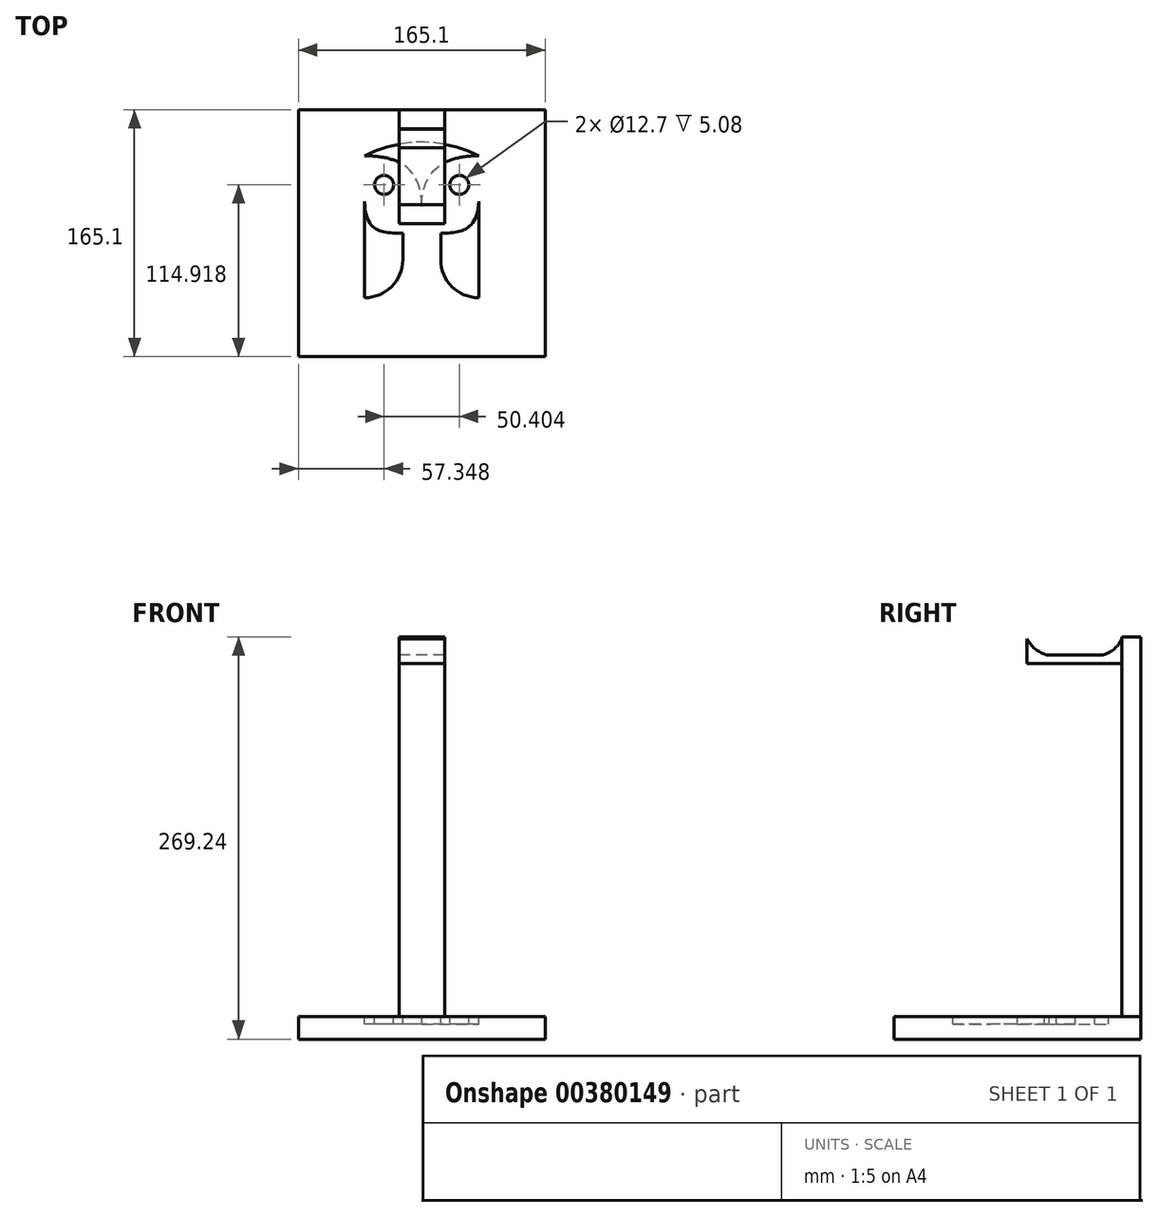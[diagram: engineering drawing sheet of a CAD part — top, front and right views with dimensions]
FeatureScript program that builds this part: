
annotation { "Feature Type Name" : "Feature", "Feature Type Description" : "" }
export const myFeature = defineFeature(function(context is Context, id is Id, definition is map)
    precondition{}
    {
        {
            var Q0;
            Q0=qCreatedBy(makeId("Front.planeOp"),FACE);
            var sketch = newSketch(context, id + "F0", { "sketchPlane" : qUnion([Q0])});
            skLineSegment(sketch, "E0.bottom", {"start": v(82.55, 7.62) * mm, "end": v(-82.55, 7.62) * mm});
            skLineSegment(sketch, "E0.top", {"start": v(82.55, -7.62) * mm, "end": v(-82.55, -7.62) * mm});
            skLineSegment(sketch, "E0.left", {"start": v(82.55, 7.62) * mm, "end": v(82.55, -7.62) * mm});
            skLineSegment(sketch, "E0.right", {"start": v(-82.55, 7.62) * mm, "end": v(-82.55, -7.62) * mm});
            skPoint(sketch, "E0.middle", {"position": v(0, 0) * mm});
            skSolve(sketch);
        }
        {
            var Q0;
            Q0 = qSketchRegion(id + "F0", true);
            extrude(context, id + "F1", {"entities" : qUnion([Q0]), "endBound" : BoundingType.SYMMETRIC, "oppositeDirection" : true, "depth" : 165.1 * mm});
        }
        {
            var Q0;
            Q0=makeQuery(id+"F1.opExtrude","SWEPT_FACE",FACE,{"disambiguationData":[OSD([sQuery(id+"F0.wireOp",EDGE,"E0.bottom")])]});
            var sketch = newSketch(context, id + "F2", { "sketchPlane" : qUnion([Q0])});
            skLineSegment(sketch, "E1.bottom", {"start": v(-15.24, 82.55) * mm, "end": v(15.24, 82.55) * mm});
            skLineSegment(sketch, "E1.top", {"start": v(-15.24, 69.85) * mm, "end": v(15.24, 69.85) * mm});
            skLineSegment(sketch, "E1.left", {"start": v(-15.24, 82.55) * mm, "end": v(-15.24, 69.85) * mm});
            skLineSegment(sketch, "E1.right", {"start": v(15.24, 82.55) * mm, "end": v(15.24, 69.85) * mm});
            skLineSegment(sketch, "E2.bottom", {"start": v(-38.1, 0) * mm, "end": v(-12.7, 0) * mm});
            skLineSegment(sketch, "E2.top", {"start": v(-38.1, -17.78) * mm, "end": v(-12.7, -17.78) * mm});
            skLineSegment(sketch, "E2.left", {"start": v(-38.1, 0) * mm, "end": v(-38.1, -17.78) * mm});
            skLineSegment(sketch, "E2.right", {"start": v(-12.7, 0) * mm, "end": v(-12.7, -17.78) * mm});
            skLineSegment(sketch, "E3.bottom", {"start": v(12.7, 0) * mm, "end": v(38.1, 0) * mm});
            skLineSegment(sketch, "E3.top", {"start": v(12.7, -17.78) * mm, "end": v(38.1, -17.78) * mm});
            skLineSegment(sketch, "E3.left", {"start": v(12.7, 0) * mm, "end": v(12.7, -17.78) * mm});
            skLineSegment(sketch, "E3.right", {"start": v(38.1, 0) * mm, "end": v(38.1, -17.78) * mm});
            skArc(sketch, "E4", {"start": v(-12.7, -17.78) * mm, "mid": v(-20.14, -35.74) * mm, "end": v(-38.1, -43.18) * mm});
            skLineSegment(sketch, "E5", {"start": v(-38.1, -17.78) * mm, "end": v(-38.1, -43.18) * mm});
            skArc(sketch, "E6", {"start": v(12.7, -17.78) * mm, "mid": v(20.14, -35.74) * mm, "end": v(38.1, -43.18) * mm});
            skLineSegment(sketch, "E7", {"start": v(38.1, -17.78) * mm, "end": v(38.1, -43.18) * mm});
            skLineSegment(sketch, "E8", {"start": v(38.1, 0) * mm, "end": v(38.1, 21.23) * mm});
            skLineSegment(sketch, "E9", {"start": v(-38.1, 0) * mm, "end": v(-38.1, 21.23) * mm});
            skFitSpline(sketch, "E10", {"points": [v(-12.7, 0) * mm, v(-38.1, 21.23) * mm], "startDerivative": vector(-38.1, 0) * mm, "endDerivative": vector(0, 63.68) * mm});
            skFitSpline(sketch, "E11", {"points": [v(38.1, 21.23) * mm, v(12.7, 0) * mm], "startDerivative": vector(0, -63.68) * mm, "endDerivative": vector(-27.64, 0) * mm});
            skLineSegment(sketch, "E12", {"start": v(-10.78, 17.94) * mm, "end": v(0, 7.17) * mm});
            skLineSegment(sketch, "E13", {"start": v(0, 7.17) * mm, "end": v(10.78, 17.94) * mm});
            skLineSegment(sketch, "E14", {"start": v(-10.78, 17.94) * mm, "end": v(10.78, 17.94) * mm});
            skCircle(sketch, "E15", {"center": v(25.2, 32.37) * mm, "radius": 6.35 * mm});
            skCircle(sketch, "E16", {"center": v(-25.2, 32.37) * mm, "radius": 6.35 * mm});
            skPoint(sketch, "E17", {"position": v(0, 17.94) * mm});
            skPoint(sketch, "E18", {"position": v(38.1, 51.82) * mm});
            skPoint(sketch, "E19", {"position": v(-38.1, 51.82) * mm});
            skFitSpline(sketch, "E20", {"points": [v(0, 17.94) * mm, v(-38.1, 51.82) * mm], "startDerivative": vector(0, 62.62) * mm, "endDerivative": vector(-84.2, 0) * mm});
            skFitSpline(sketch, "E21", {"points": [v(0, 17.94) * mm, v(38.1, 51.82) * mm], "startDerivative": vector(0, 62.62) * mm, "endDerivative": vector(80.13, 0) * mm});
            skArc(sketch, "E22", {"start": v(38.1, 51.82) * mm, "mid": v(0, 60.9) * mm, "end": v(-38.1, 51.82) * mm});
            skSolve(sketch);
        }
        {
            var Q0;
            Q0=makeQuery(id+"F2.imprint","IMPRINT",FACE,{"disambiguationData":[TD([[makeQuery(id+"F2.imprint","IMPRINT",EDGE,{"derivedFrom":sQuery(id+"F2.wireOp",EDGE,"E1.bottom")}),1.0]])]});
            extrude(context, id + "F3", {"entities" : qUnion([Q0]), "operationType" : NewBodyOperationType.ADD, "depth" : 254 * mm});
        }
        {
            var Q0;
            Q0=qCreatedBy(makeId("Right.planeOp"),FACE);
            var sketch = newSketch(context, id + "F4", { "sketchPlane" : qUnion([Q0])});
            skLineSegment(sketch, "E23.bottom", {"start": v(69.82, 249.55) * mm, "end": v(6.32, 249.55) * mm});
            skLineSegment(sketch, "E23.top", {"start": v(69.82, 243.6) * mm, "end": v(6.32, 243.6) * mm});
            skLineSegment(sketch, "E23.left", {"start": v(69.82, 249.55) * mm, "end": v(69.82, 243.6) * mm});
            skLineSegment(sketch, "E23.right", {"start": v(6.32, 249.55) * mm, "end": v(6.32, 243.6) * mm});
            skPoint(sketch, "E24", {"position": v(69.67, 260.1) * mm});
            skLineSegment(sketch, "E25", {"start": v(6.32, 249.55) * mm, "end": v(6.32, 260.1) * mm});
            skPoint(sketch, "E26", {"position": v(19.02, 249.55) * mm});
            skPoint(sketch, "E27", {"position": v(57.12, 249.55) * mm});
            skArc(sketch, "E28", {"start": v(57.12, 249.55) * mm, "mid": v(64.62, 253.37) * mm, "end": v(69.67, 260.1) * mm});
            skArc(sketch, "E29", {"start": v(6.32, 260.1) * mm, "mid": v(11.7, 253.65) * mm, "end": v(19.02, 249.55) * mm});
            skLineSegment(sketch, "E30", {"start": v(69.67, 260.1) * mm, "end": v(69.82, 249.55) * mm});
            skSolve(sketch);
        }
        {
            var Q0;
            Q0 = qSketchRegion(id + "F4", true);
            extrude(context, id + "F5", {"entities" : qUnion([Q0]), "endBound" : BoundingType.SYMMETRIC, "depth" : 30.48 * mm});
        }
        {
            var Q0;
            {var subQ0=sQuery(id+"F2.wireOp",EDGE,"E20");Q0=makeQuery(id+"F2.imprint","IMPRINT",FACE,{"disambiguationData":[TD([[makeQuery(id+"F2.imprint","IMPRINT",EDGE,{"derivedFrom":subQ0}),-1.0]])]});}
            var Q1;
            Q1=makeQuery(id+"F2.imprint","IMPRINT",FACE,{"disambiguationData":[TD([[makeQuery(id+"F2.imprint","IMPRINT",EDGE,{"derivedFrom":sQuery(id+"F2.wireOp",EDGE,"E16")}),1.0]])]});
            var Q2;
            Q2=makeQuery(id+"F2.imprint","IMPRINT",FACE,{"disambiguationData":[TD([[makeQuery(id+"F2.imprint","IMPRINT",EDGE,{"derivedFrom":sQuery(id+"F2.wireOp",EDGE,"E15")}),1.0]])]});
            var Q3;
            Q3=makeQuery(id+"F2.imprint","IMPRINT",FACE,{"disambiguationData":[TD([[makeQuery(id+"F2.imprint","IMPRINT",EDGE,{"derivedFrom":sQuery(id+"F2.wireOp",EDGE,"E2.bottom")}),-1.0]])]});
            var Q4;
            Q4=makeQuery(id+"F2.imprint","IMPRINT",FACE,{"disambiguationData":[TD([[makeQuery(id+"F2.imprint","IMPRINT",EDGE,{"derivedFrom":sQuery(id+"F2.wireOp",EDGE,"E2.top")}),-1.0]])]});
            var Q5;
            Q5=makeQuery(id+"F2.imprint","IMPRINT",FACE,{"disambiguationData":[TD([[makeQuery(id+"F2.imprint","IMPRINT",EDGE,{"derivedFrom":sQuery(id+"F2.wireOp",EDGE,"E2.bottom")}),1.0]])]});
            var Q6;
            Q6=makeQuery(id+"F2.imprint","IMPRINT",FACE,{"disambiguationData":[TD([[makeQuery(id+"F2.imprint","IMPRINT",EDGE,{"derivedFrom":sQuery(id+"F2.wireOp",EDGE,"E3.bottom")}),1.0]])]});
            var Q7;
            Q7=makeQuery(id+"F2.imprint","IMPRINT",FACE,{"disambiguationData":[TD([[makeQuery(id+"F2.imprint","IMPRINT",EDGE,{"derivedFrom":sQuery(id+"F2.wireOp",EDGE,"E3.bottom")}),-1.0]])]});
            var Q8;
            Q8=makeQuery(id+"F2.imprint","IMPRINT",FACE,{"disambiguationData":[TD([[makeQuery(id+"F2.imprint","IMPRINT",EDGE,{"derivedFrom":sQuery(id+"F2.wireOp",EDGE,"E3.top")}),-1.0]])]});
            extrude(context, id + "F6", {"entities" : qUnion([Q0, Q1, Q2, Q3, Q4, Q5, Q6, Q7, Q8]), "operationType" : NewBodyOperationType.REMOVE, "oppositeDirection" : true, "depth" : 5.08 * mm});
        }
    });
